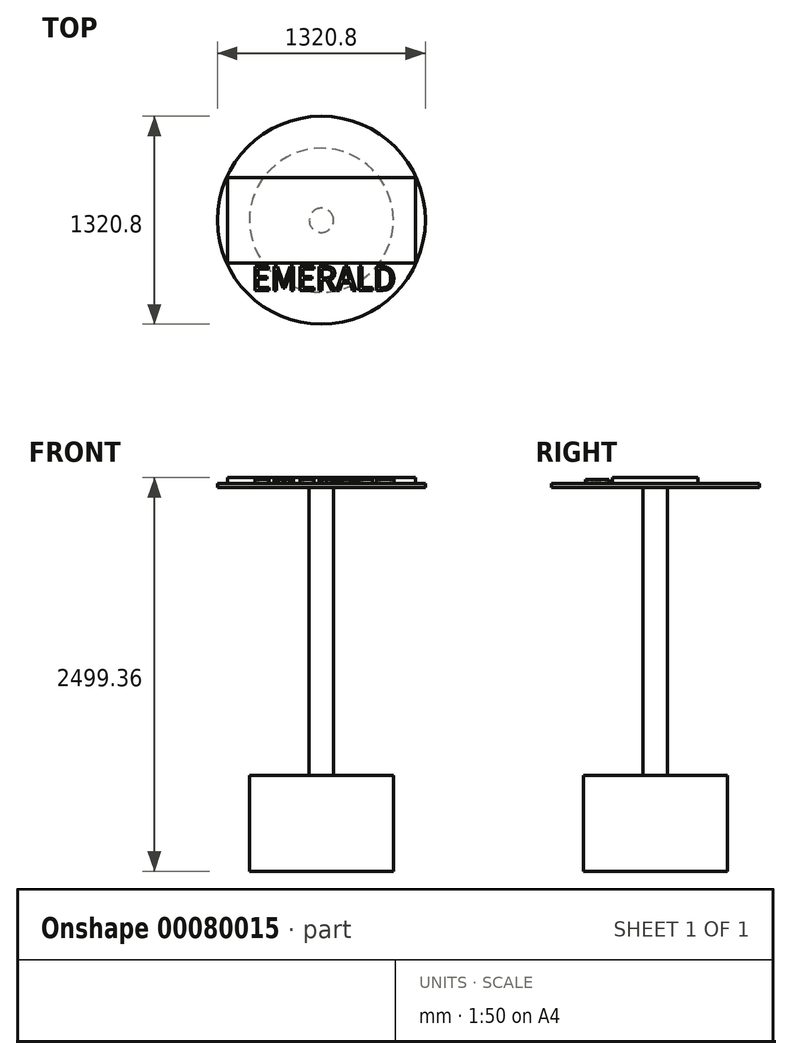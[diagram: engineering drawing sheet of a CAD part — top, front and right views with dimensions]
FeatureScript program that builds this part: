
annotation { "Feature Type Name" : "Feature", "Feature Type Description" : "" }
export const myFeature = defineFeature(function(context is Context, id is Id, definition is map)
    precondition{}
    {
        {
            var Q0;
            Q0=qCreatedBy(makeId("Front.planeOp"),FACE);
            var sketch = newSketch(context, id + "F0", { "sketchPlane" : qUnion([Q0])});
            skLineSegment(sketch, "E0.bottom", {"start": v(457.2, -798.24) * mm, "end": v(-457.2, -798.24) * mm});
            skLineSegment(sketch, "E0.top", {"start": v(457.2, -1407.84) * mm, "end": v(-457.2, -1407.84) * mm});
            skLineSegment(sketch, "E0.left", {"start": v(457.2, -798.24) * mm, "end": v(457.2, -1407.84) * mm});
            skLineSegment(sketch, "E0.right", {"start": v(-457.2, -798.24) * mm, "end": v(-457.2, -1407.84) * mm});
            skPoint(sketch, "E0.middle", {"position": v(0, -1103.04) * mm});
            skLineSegment(sketch, "E1.bottom", {"start": v(77.16, -798.24) * mm, "end": v(-77.16, -798.24) * mm});
            skLineSegment(sketch, "E1.left", {"start": v(77.16, -798.24) * mm, "end": v(77.16, 1030.56) * mm});
            skLineSegment(sketch, "E1.right", {"start": v(-77.16, -798.24) * mm, "end": v(-77.16, 1030.56) * mm});
            skPoint(sketch, "E1.middle", {"position": v(0, 116.16) * mm});
            skLineSegment(sketch, "E2", {"start": v(-77.16, 1030.56) * mm, "end": v(77.16, 1030.56) * mm});
            skLineSegment(sketch, "E3.bottom", {"start": v(77.16, 1030.56) * mm, "end": v(-77.16, 1030.56) * mm});
            skLineSegment(sketch, "E3.top", {"start": v(77.16, 1091.52) * mm, "end": v(-77.16, 1091.52) * mm});
            skPoint(sketch, "E3.middle", {"position": v(0, 1061.04) * mm});
            skLineSegment(sketch, "E4.bottom", {"start": v(-596.9, 1030.56) * mm, "end": v(596.9, 1030.56) * mm});
            skLineSegment(sketch, "E4.top", {"start": v(-596.9, 1091.52) * mm, "end": v(596.9, 1091.52) * mm});
            skLineSegment(sketch, "E4.left", {"start": v(-596.9, 1030.56) * mm, "end": v(-596.9, 1091.52) * mm});
            skLineSegment(sketch, "E4.right", {"start": v(596.9, 1030.56) * mm, "end": v(596.9, 1091.52) * mm});
            skLineSegment(sketch, "E5", {"start": v(0, -1103.04) * mm, "end": v(0, 1061.04) * mm});
            skLineSegment(sketch, "E6", {"start": v(0, -1103.04) * mm, "end": v(0, -1407.84) * mm});
            skLineSegment(sketch, "E7.bottom", {"start": v(660.4, 1030.56) * mm, "end": v(-660.4, 1030.56) * mm});
            skLineSegment(sketch, "E7.top", {"start": v(660.4, 1055.96) * mm, "end": v(-660.4, 1055.96) * mm});
            skLineSegment(sketch, "E7.left", {"start": v(660.4, 1030.56) * mm, "end": v(660.4, 1055.96) * mm});
            skLineSegment(sketch, "E7.right", {"start": v(-660.4, 1030.56) * mm, "end": v(-660.4, 1055.96) * mm});
            skPoint(sketch, "E7.middle", {"position": v(0, 1043.26) * mm});
            skSolve(sketch);
        }
        {
            var Q0;
            {var subQ5=sQuery(id+"F0.wireOp",EDGE,"E0.right");Q0=makeQuery(id+"F0.imprint","IMPRINT",FACE,{"disambiguationData":[TD([[makeQuery(id+"F0.imprint","IMPRINT",EDGE,{"derivedFrom":subQ5}),1.0]])]});}
            var Q1;
            {var subQ0=sQuery(id+"F0.wireOp",EDGE,"E1.right");Q1=makeQuery(id+"F0.imprint","IMPRINT",FACE,{"disambiguationData":[TD([[makeQuery(id+"F0.imprint","IMPRINT",EDGE,{"derivedFrom":subQ0}),-1.0]])]});}
            var Q2;
            Q2=sQuery(id+"F0.wireOp",EDGE,"E5");
            revolve(context, id + "F1", {"entities" : qUnion([Q0, Q1]), "axis" : qUnion([Q2]), "revolveType" : RevolveType.FULL});
        }
        {
            var Q0;
            {var subQ1=sQuery(id+"F0.wireOp",EDGE,"E4.top");var subQ5=sQuery(id+"F0.wireOp",EDGE,"E4.left");var subQ6=makeQuery(id+"F0.imprint","INTERSECT",VERTEX,{"derivedFrom":[subQ1,subQ5]});Q0=makeQuery(id+"F0.imprint","IMPRINT",FACE,{"disambiguationData":[TD([[makeQuery(id+"F0.imprint","IMPRINT",EDGE,{"disambiguationData":[TD([[subQ6,-1.0]])],"derivedFrom":subQ1}),-1.0]])]});}
            extrude(context, id + "F2", {"entities" : qUnion([Q0]), "endBound" : BoundingType.SYMMETRIC, "depth" : 541.02 * mm});
        }
        {
            var Q0;
            {var subQ0=sQuery(id+"F0.wireOp",EDGE,"E7.bottom");var subQ4=sQuery(id+"F0.wireOp",EDGE,"E4.right");var subQ5=makeQuery(id+"F0.imprint","INTERSECT",VERTEX,{"derivedFrom":[subQ4,subQ0]});Q0=makeQuery(id+"F0.imprint","IMPRINT",FACE,{"disambiguationData":[TD([[makeQuery(id+"F0.imprint","IMPRINT",EDGE,{"disambiguationData":[TD([[subQ5,-1.0]])],"derivedFrom":subQ4}),1.0]])]});}
            var Q1;
            {var subQ5=sQuery(id+"F0.wireOp",EDGE,"E7.left");Q1=makeQuery(id+"F0.imprint","IMPRINT",FACE,{"disambiguationData":[TD([[makeQuery(id+"F0.imprint","IMPRINT",EDGE,{"derivedFrom":subQ5}),1.0]])]});}
            var Q2;
            Q2=sQuery(id+"F0.wireOp",EDGE,"E5");
            revolve(context, id + "F3", {"entities" : qUnion([Q0, Q1]), "axis" : qUnion([Q2]), "revolveType" : RevolveType.FULL});
        }
        {
            var Q0;
            Q0=makeQuery(id+"F3.opRevolve","SWEPT_FACE",FACE,{"disambiguationData":[OSD([sQuery(id+"F0.wireOp",EDGE,"E7.top")])]});
            var sketch = newSketch(context, id + "F4", { "sketchPlane" : qUnion([Q0])});
            skText(sketch, "E8", { "text": "EMERALD", "fontName": "NotoSansCJKjp-Regular.otf"});
            const initialGuessF4  = {"E8": [-0.44222, -0.44495, 1, 0, 0.14755]};
            skSetInitialGuess(sketch, initialGuessF4);
            skSolve(sketch);
        }
        {
            var Q0;
            Q0=makeQuery(id+"F4.imprint","IMPRINT",FACE,{"disambiguationData":[TD([[makeQuery(id+"F4.imprint","IMPRINT",EDGE,{"derivedFrom":sQuery(id+"F4.wireOp",EDGE,"E8.sketch_text.stroke-46")}),1.0]])]});
            var Q1;
            Q1=makeQuery(id+"F4.imprint","IMPRINT",FACE,{"disambiguationData":[TD([[makeQuery(id+"F4.imprint","IMPRINT",EDGE,{"derivedFrom":sQuery(id+"F4.wireOp",EDGE,"E8.sketch_text.stroke-81")}),1.0]])]});
            var Q2;
            Q2=makeQuery(id+"F4.imprint","IMPRINT",FACE,{"disambiguationData":[TD([[makeQuery(id+"F4.imprint","IMPRINT",EDGE,{"derivedFrom":sQuery(id+"F4.wireOp",EDGE,"E8.sketch_text.stroke-34")}),1.0]])]});
            var Q3;
            Q3=makeQuery(id+"F4.imprint","IMPRINT",FACE,{"disambiguationData":[TD([[makeQuery(id+"F4.imprint","IMPRINT",EDGE,{"derivedFrom":sQuery(id+"F4.wireOp",EDGE,"E8.sketch_text.stroke-0")}),1.0]])]});
            var Q4;
            Q4=makeQuery(id+"F4.imprint","IMPRINT",FACE,{"disambiguationData":[TD([[makeQuery(id+"F4.imprint","IMPRINT",EDGE,{"derivedFrom":sQuery(id+"F4.wireOp",EDGE,"E8.sketch_text.stroke-61")}),1.0]])]});
            var Q5;
            Q5=makeQuery(id+"F4.imprint","IMPRINT",FACE,{"disambiguationData":[TD([[makeQuery(id+"F4.imprint","IMPRINT",EDGE,{"derivedFrom":sQuery(id+"F4.wireOp",EDGE,"E8.sketch_text.stroke-75")}),1.0]])]});
            var Q6;
            Q6=makeQuery(id+"F4.imprint","IMPRINT",FACE,{"disambiguationData":[TD([[makeQuery(id+"F4.imprint","IMPRINT",EDGE,{"derivedFrom":sQuery(id+"F4.wireOp",EDGE,"E8.sketch_text.stroke-12")}),1.0]])]});
            extrude(context, id + "F5", {"entities" : qUnion([Q0, Q1, Q2, Q3, Q4, Q5, Q6]), "operationType" : NewBodyOperationType.ADD, "depth" : 25.4 * mm});
        }
    });
